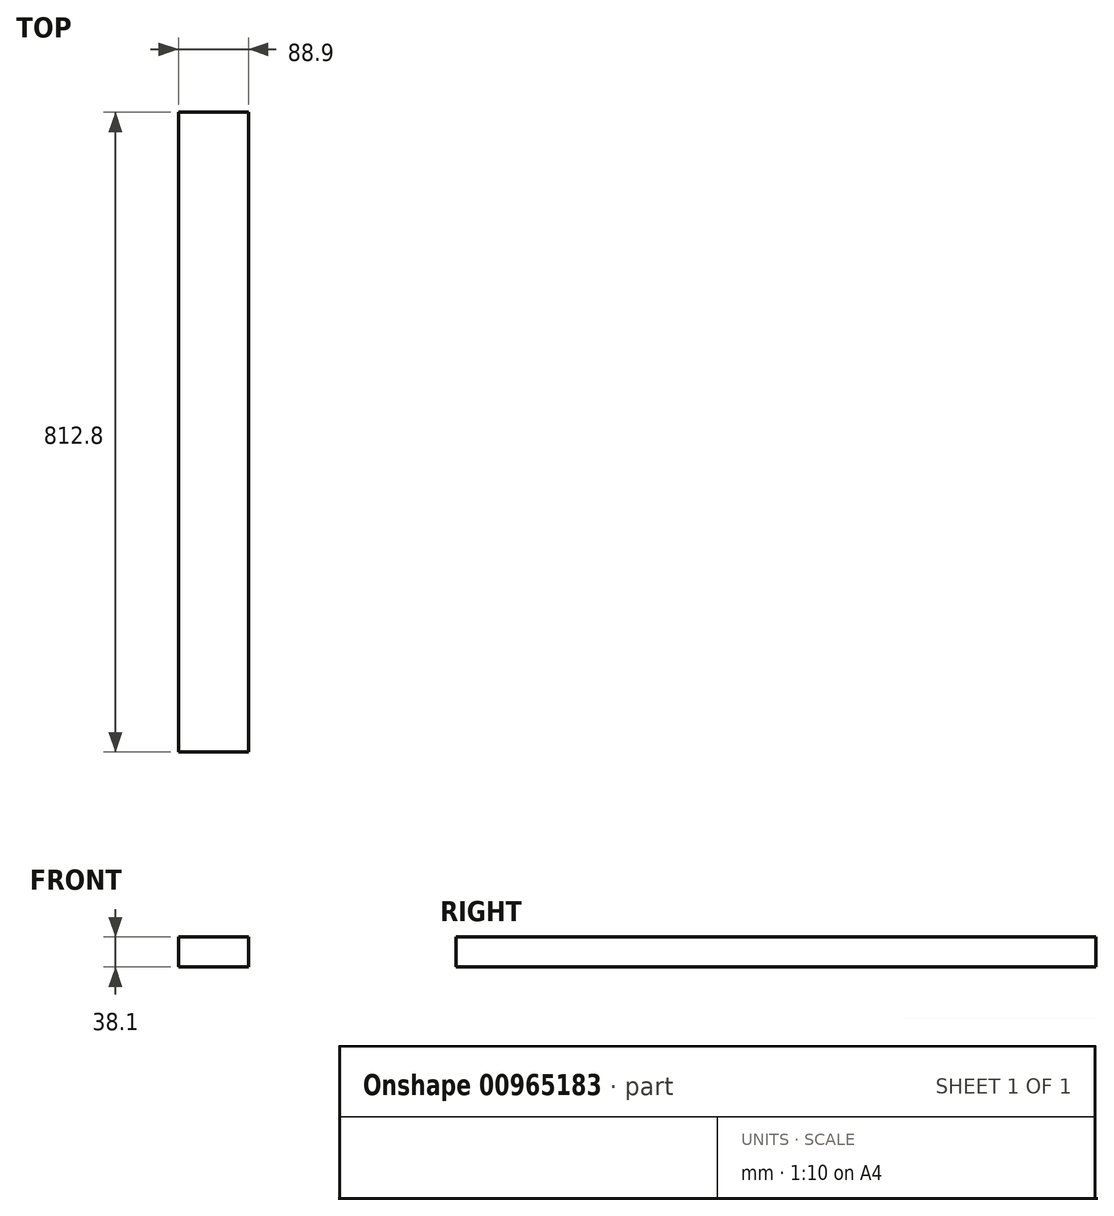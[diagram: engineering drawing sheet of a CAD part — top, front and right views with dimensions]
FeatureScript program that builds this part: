
annotation { "Feature Type Name" : "Feature", "Feature Type Description" : "" }
export const myFeature = defineFeature(function(context is Context, id is Id, definition is map)
    precondition{}
    {
        {
            var Q0;
            Q0=qCreatedBy(makeId("Front.planeOp"),FACE);
            var sketch = newSketch(context, id + "F0", { "sketchPlane" : qUnion([Q0])});
            skLineSegment(sketch, "E0.bottom", {"start": v(508.1, -85.36) * mm, "end": v(597, -85.36) * mm});
            skLineSegment(sketch, "E0.top", {"start": v(508.1, -47.26) * mm, "end": v(597, -47.26) * mm});
            skLineSegment(sketch, "E0.left", {"start": v(508.1, -85.36) * mm, "end": v(508.1, -47.26) * mm});
            skLineSegment(sketch, "E0.right", {"start": v(597, -85.36) * mm, "end": v(597, -47.26) * mm});
            skSolve(sketch);
        }
        {
            var Q0;
            Q0=makeQuery(id+"F0.imprint","IMPRINT",FACE,{"disambiguationData":[TD([[makeQuery(id+"F0.imprint","IMPRINT",EDGE,{"derivedFrom":sQuery(id+"F0.wireOp",EDGE,"E0.bottom")}),1.0]])]});
            extrude(context, id + "F1", {"entities" : qUnion([Q0]), "depth" : 812.8 * mm, "offsetDistance" : 25.4 * mm});
        }
    });
